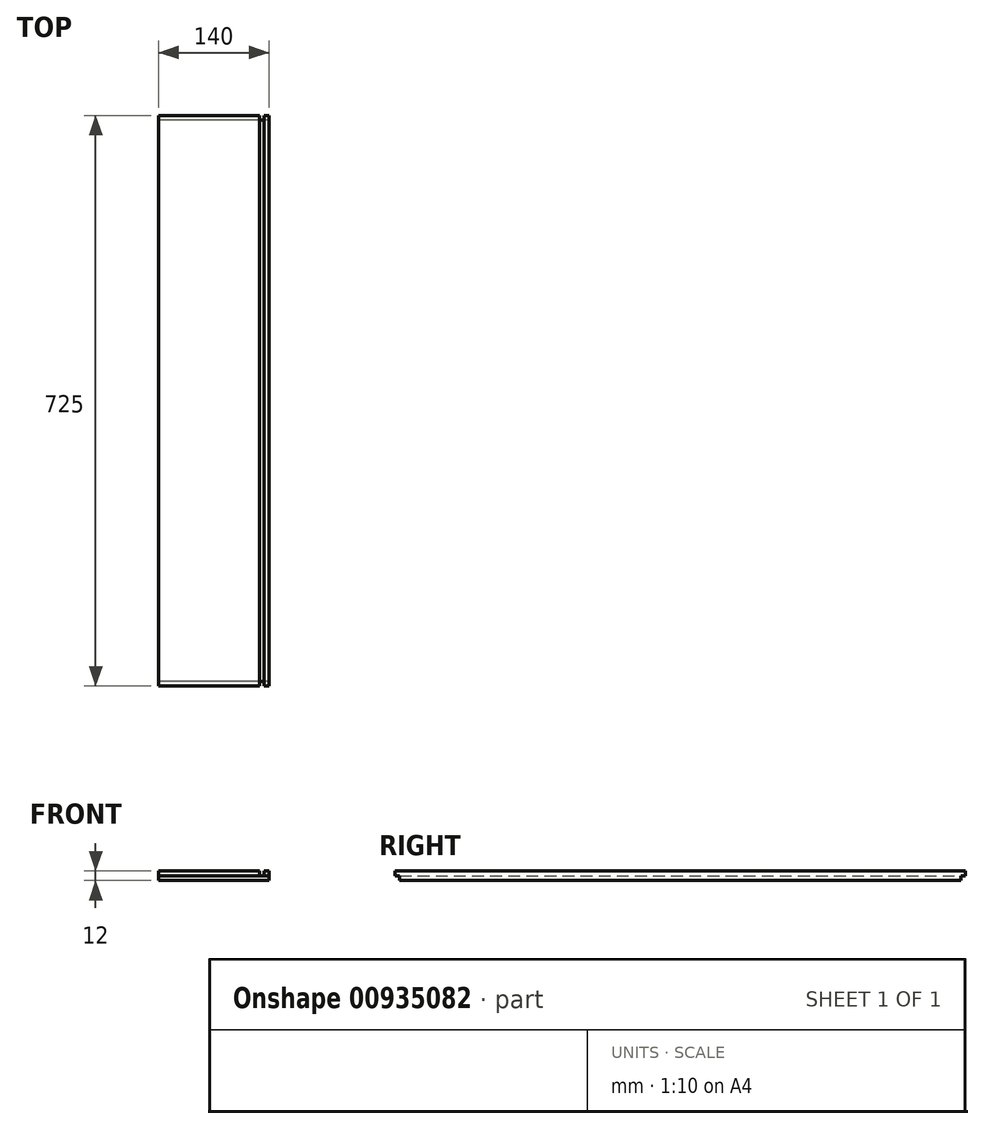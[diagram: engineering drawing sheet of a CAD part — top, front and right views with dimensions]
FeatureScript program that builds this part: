
annotation { "Feature Type Name" : "Feature", "Feature Type Description" : "" }
export const myFeature = defineFeature(function(context is Context, id is Id, definition is map)
    precondition{}
    {
        {
            var Q0;
            Q0=qCreatedBy(makeId("Front.planeOp"),FACE);
            var sketch = newSketch(context, id + "F0", { "sketchPlane" : qUnion([Q0])});
            skLineSegment(sketch, "E0.bottom", {"start": v(0, 0) * mm, "end": v(140, 0) * mm});
            skLineSegment(sketch, "E0.top", {"start": v(0, 12) * mm, "end": v(140, 12) * mm});
            skLineSegment(sketch, "E0.left", {"start": v(0, 0) * mm, "end": v(0, 12) * mm});
            skLineSegment(sketch, "E0.right", {"start": v(140, 0) * mm, "end": v(140, 12) * mm});
            skSolve(sketch);
        }
        {
            var Q0;
            Q0=makeQuery(id+"F0.imprint","IMPRINT",FACE,{"disambiguationData":[TD([[makeQuery(id+"F0.imprint","IMPRINT",EDGE,{"derivedFrom":sQuery(id+"F0.wireOp",EDGE,"E0.bottom")}),1.0]])]});
            extrude(context, id + "F1", {"entities" : qUnion([Q0]), "depth" : 725 * mm, "offsetDistance" : 25 * mm});
        }
        {
            var Q0;
            Q0=qCreatedBy(makeId("Right.planeOp"),FACE);
            var sketch = newSketch(context, id + "F2", { "sketchPlane" : qUnion([Q0])});
            skLineSegment(sketch, "E1.0", {"start": v(-725, 12) * mm, "end": v(0, 12) * mm, "construction": true});
            skLineSegment(sketch, "E2.bottom", {"start": v(-725, 6) * mm, "end": v(-719, 6) * mm});
            skLineSegment(sketch, "E2.top", {"start": v(-725, 0) * mm, "end": v(-719, 0) * mm});
            skLineSegment(sketch, "E2.left", {"start": v(-725, 6) * mm, "end": v(-725, 0) * mm});
            skLineSegment(sketch, "E2.right", {"start": v(-719, 6) * mm, "end": v(-719, 0) * mm});
            skLineSegment(sketch, "E3.bottom", {"start": v(0, 6) * mm, "end": v(-6, 6) * mm});
            skLineSegment(sketch, "E3.top", {"start": v(0, 0) * mm, "end": v(-6, 0) * mm});
            skLineSegment(sketch, "E3.left", {"start": v(0, 6) * mm, "end": v(0, 0) * mm});
            skLineSegment(sketch, "E3.right", {"start": v(-6, 6) * mm, "end": v(-6, 0) * mm});
            skLineSegment(sketch, "E4.0", {"start": v(-725, 0) * mm, "end": v(0, 0) * mm, "construction": true});
            skSolve(sketch);
        }
        {
            var Q0;
            Q0=qSketchRegion(id+"F2",true);
            extrude(context, id + "F3", {"entities" : qUnion([Q0]), "operationType" : NewBodyOperationType.REMOVE, "endBound" : BoundingType.THROUGH_ALL, "depth" : 25 * mm, "offsetDistance" : 25 * mm});
        }
        {
            var Q0;
            Q0=qCreatedBy(makeId("Front.planeOp"),FACE);
            var sketch = newSketch(context, id + "F4", { "sketchPlane" : qUnion([Q0])});
            skLineSegment(sketch, "E5.bottom", {"start": v(134, 12) * mm, "end": v(128, 12) * mm});
            skLineSegment(sketch, "E5.top", {"start": v(134, 6) * mm, "end": v(128, 6) * mm});
            skLineSegment(sketch, "E5.left", {"start": v(134, 12) * mm, "end": v(134, 6) * mm});
            skLineSegment(sketch, "E5.right", {"start": v(128, 12) * mm, "end": v(128, 6) * mm});
            skSolve(sketch);
        }
        {
            var Q0;
            Q0=qSketchRegion(id+"F4",true);
            extrude(context, id + "F5", {"entities" : qUnion([Q0]), "operationType" : NewBodyOperationType.REMOVE, "endBound" : BoundingType.THROUGH_ALL, "depth" : 25 * mm, "offsetDistance" : 25 * mm});
        }
    });
